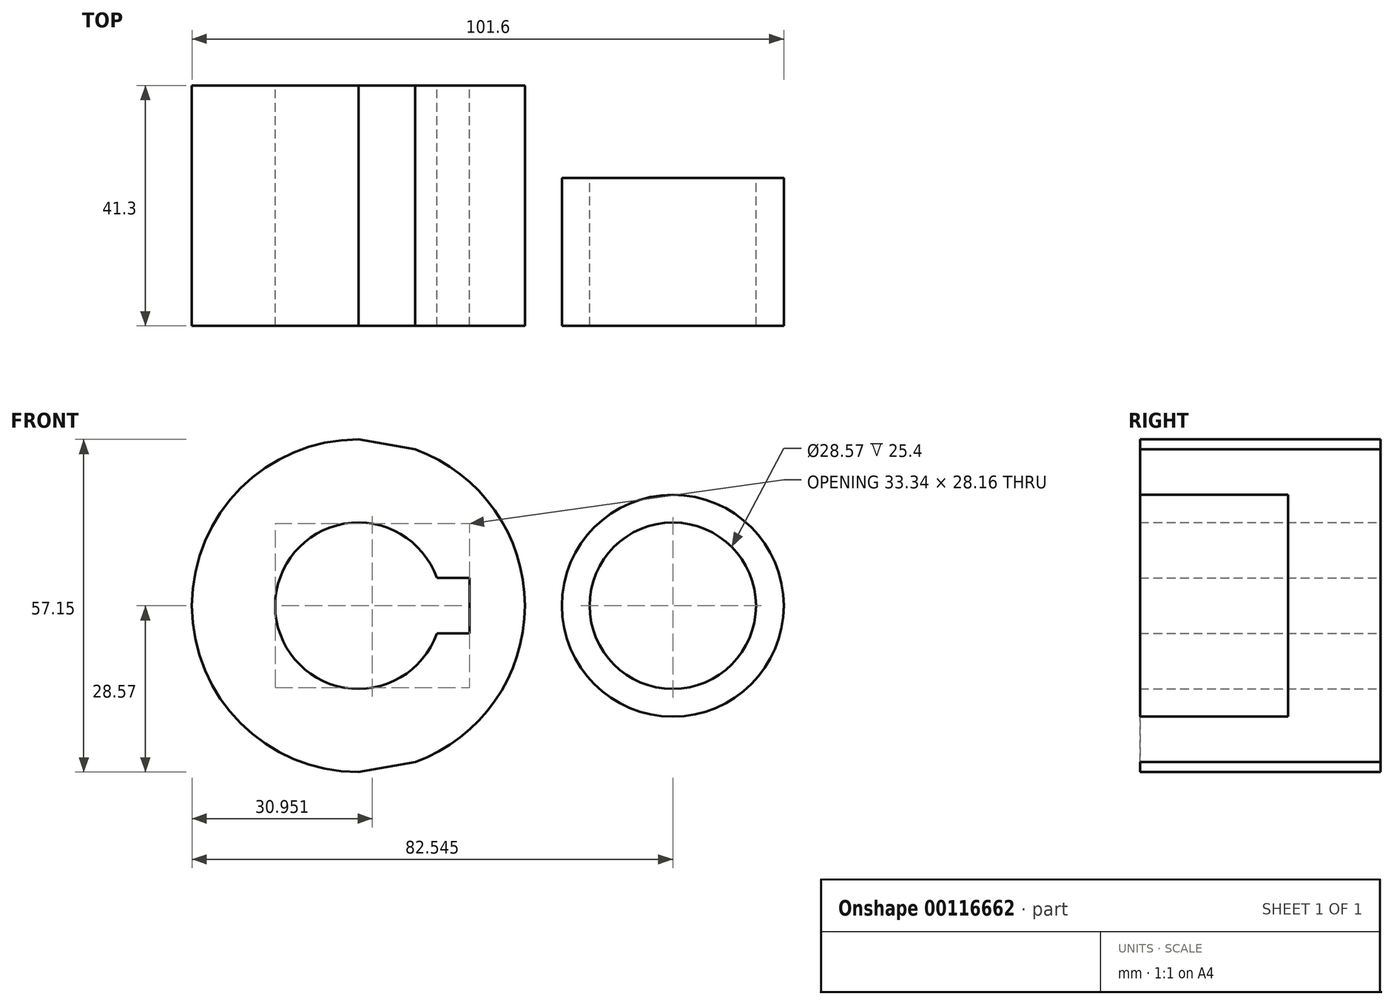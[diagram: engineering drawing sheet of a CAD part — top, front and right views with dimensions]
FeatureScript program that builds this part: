
annotation { "Feature Type Name" : "Feature", "Feature Type Description" : "" }
export const myFeature = defineFeature(function(context is Context, id is Id, definition is map)
    precondition{}
    {
        {
            var Q0;
            Q0=qCreatedBy(makeId("Front.planeOp"),FACE);
            var sketch = newSketch(context, id + "F0", { "sketchPlane" : qUnion([Q0])});
            skCircle(sketch, "E0", {"center": v(0, 0) * mm, "radius": 28.58 * mm});
            skCircle(sketch, "E1", {"center": v(53.98, 0) * mm, "radius": 19.05 * mm});
            skLineSegment(sketch, "E2", {"start": v(0, 28.58) * mm, "end": v(54.16, 19.05) * mm});
            skLineSegment(sketch, "E3", {"start": v(0, -28.58) * mm, "end": v(53.97, -19.05) * mm});
            skCircle(sketch, "E4", {"center": v(0, 0) * mm, "radius": 14.29 * mm});
            skCircle(sketch, "E5", {"center": v(53.98, 0) * mm, "radius": 14.29 * mm});
            skLineSegment(sketch, "E6.bottom", {"start": v(19.05, -4.76) * mm, "end": v(-19.05, -4.76) * mm});
            skLineSegment(sketch, "E6.top", {"start": v(19.05, 4.76) * mm, "end": v(-19.05, 4.76) * mm});
            skLineSegment(sketch, "E6.left", {"start": v(19.05, -4.76) * mm, "end": v(19.05, 4.76) * mm});
            skLineSegment(sketch, "E6.right", {"start": v(-19.05, -4.76) * mm, "end": v(-19.05, 4.76) * mm});
            skSolve(sketch);
        }
        {
            var Q0;
            {var subQ4=sQuery(id+"F0.wireOp",EDGE,"E6.left");Q0=makeQuery(id+"F0.imprint","IMPRINT",FACE,{"disambiguationData":[TD([[makeQuery(id+"F0.imprint","IMPRINT",EDGE,{"derivedFrom":subQ4}),-1.0]])]});}
            var Q1;
            {var subQ5=sQuery(id+"F0.wireOp",EDGE,"E6.right");Q1=makeQuery(id+"F0.imprint","IMPRINT",FACE,{"disambiguationData":[TD([[makeQuery(id+"F0.imprint","IMPRINT",EDGE,{"derivedFrom":subQ5}),-1.0]])]});}
            var Q2;
            {var subQ0=sQuery(id+"F0.wireOp",EDGE,"E2");var subQ1=sQuery(id+"F0.wireOp",EDGE,"E0");var subQ2=makeQuery(id+"F0.imprint","INTERSECT",VERTEX,{"disambiguationData":[OD(1.0)],"derivedFrom":[subQ1,subQ0]});Q2=makeQuery(id+"F0.imprint","IMPRINT",FACE,{"disambiguationData":[TD([[makeQuery(id+"F0.imprint","IMPRINT",EDGE,{"disambiguationData":[TD([[subQ2,1.0]])],"derivedFrom":subQ1}),-1.0]])]});}
            var Q3;
            Q3=makeQuery(id+"F0.imprint","IMPRINT",FACE,{"disambiguationData":[TD([[makeQuery(id+"F0.imprint","IMPRINT",EDGE,{"derivedFrom":sQuery(id+"F0.wireOp",EDGE,"E5")}),-1.0]])]});
            extrude(context, id + "F1", {"entities" : qUnion([Q0, Q1, Q2, Q3]), "depth" : 25.4 * mm});
        }
        {
            var Q0;
            {var subQ4=sQuery(id+"F0.wireOp",EDGE,"E6.left");Q0=makeQuery(id+"F0.imprint","IMPRINT",FACE,{"disambiguationData":[TD([[makeQuery(id+"F0.imprint","IMPRINT",EDGE,{"derivedFrom":subQ4}),-1.0]])]});}
            var Q1;
            {var subQ5=sQuery(id+"F0.wireOp",EDGE,"E6.right");Q1=makeQuery(id+"F0.imprint","IMPRINT",FACE,{"disambiguationData":[TD([[makeQuery(id+"F0.imprint","IMPRINT",EDGE,{"derivedFrom":subQ5}),-1.0]])]});}
            extrude(context, id + "F2", {"entities" : qUnion([Q0, Q1]), "operationType" : NewBodyOperationType.ADD, "oppositeDirection" : true, "depth" : 15.9 * mm});
        }
    });
